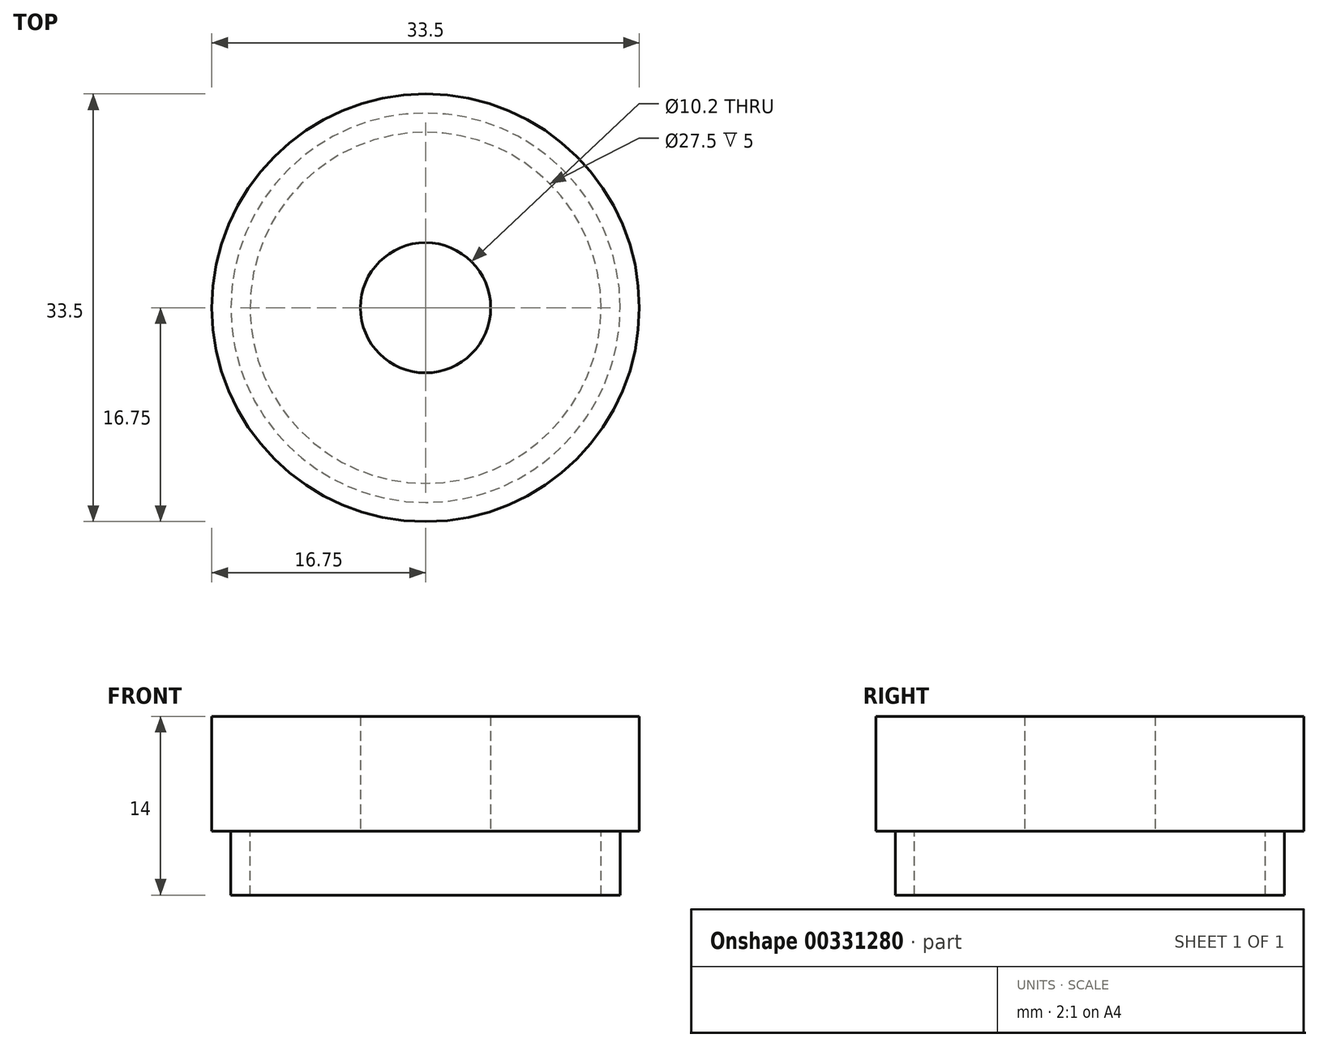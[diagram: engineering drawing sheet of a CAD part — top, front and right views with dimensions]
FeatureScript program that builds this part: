
annotation { "Feature Type Name" : "Feature", "Feature Type Description" : "" }
export const myFeature = defineFeature(function(context is Context, id is Id, definition is map)
    precondition{}
    {
        {
            var Q0;
            Q0=qCreatedBy(makeId("Top.planeOp"),FACE);
            var sketch = newSketch(context, id + "F0", { "sketchPlane" : qUnion([Q0])});
            skCircle(sketch, "E0", {"center": v(0, 0) * mm, "radius": 5.1 * mm});
            skCircle(sketch, "E1", {"center": v(0, 0) * mm, "radius": 16.75 * mm});
            skSolve(sketch);
        }
        {
            var Q0;
            Q0=makeQuery(id+"F0.imprint","IMPRINT",FACE,{"disambiguationData":[TD([[makeQuery(id+"F0.imprint","IMPRINT",EDGE,{"derivedFrom":sQuery(id+"F0.wireOp",EDGE,"E0")}),-1.0]])]});
            extrude(context, id + "F1", {"entities" : qUnion([Q0]), "depth" : 9 * mm});
        }
        {
            var Q0;
            Q0=makeQuery(id+"F1.opExtrude","CAP_FACE",FACE,{"disambiguationData":[OSD([sQuery(id+"F0.wireOp",EDGE,"E0"),sQuery(id+"F0.wireOp",EDGE,"E1")])],"isStart":true});
            var sketch = newSketch(context, id + "F2", { "sketchPlane" : qUnion([Q0])});
            skCircle(sketch, "E2", {"center": v(0, 0) * mm, "radius": 13.75 * mm});
            skCircle(sketch, "E3", {"center": v(0, 0) * mm, "radius": 15.25 * mm});
            skSolve(sketch);
        }
        {
            var Q0;
            Q0 = qSketchRegion(id + "F2", true);
            extrude(context, id + "F3", {"entities" : qUnion([Q0]), "operationType" : NewBodyOperationType.ADD, "depth" : 5 * mm});
        }
    });
